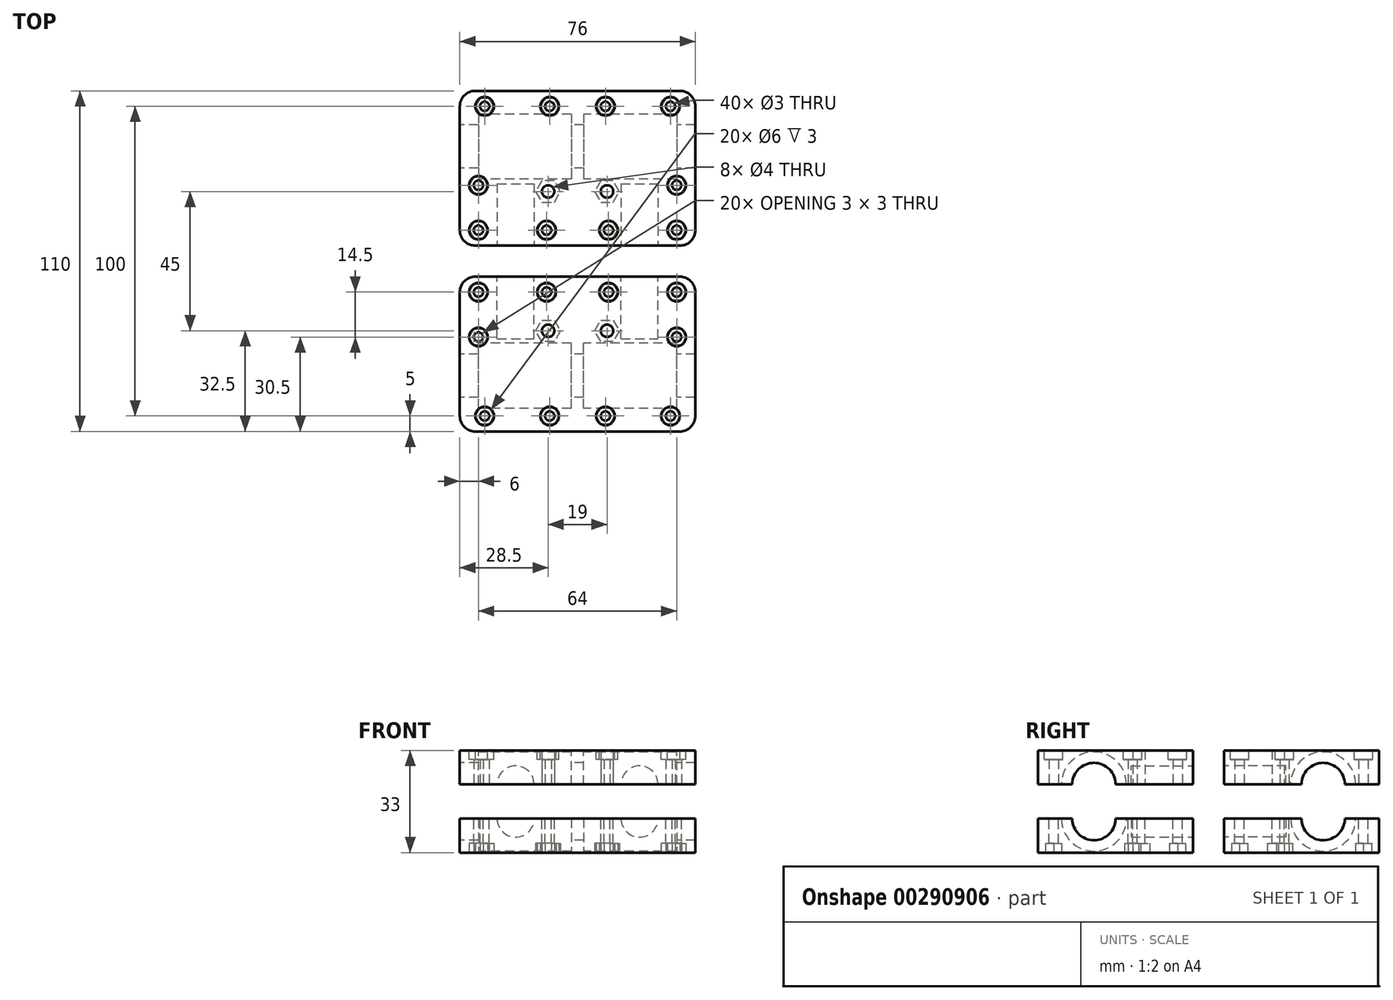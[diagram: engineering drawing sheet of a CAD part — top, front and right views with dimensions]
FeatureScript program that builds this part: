
annotation { "Feature Type Name" : "Feature", "Feature Type Description" : "" }
export const myFeature = defineFeature(function(context is Context, id is Id, definition is map)
    precondition{}
    {
        {
            var Q0;
            Q0=qCreatedBy(makeId("Top.planeOp"),FACE);
            var sketch = newSketch(context, id + "F0", { "sketchPlane" : qUnion([Q0])});
            skLineSegment(sketch, "E0.bottom", {"start": v(38, -25) * mm, "end": v(-38, -25) * mm});
            skLineSegment(sketch, "E0.top", {"start": v(38, 25) * mm, "end": v(-38, 25) * mm});
            skLineSegment(sketch, "E0.left", {"start": v(38, -25) * mm, "end": v(38, 25) * mm});
            skLineSegment(sketch, "E0.right", {"start": v(-38, -25) * mm, "end": v(-38, 25) * mm});
            skPoint(sketch, "E0.middle", {"position": v(0, 0) * mm});
            skSolve(sketch);
        }
        {
            var Q0;
            Q0 = qSketchRegion(id + "F0", true);
            extrude(context, id + "F1", {"entities" : qUnion([Q0]), "endBound" : BoundingType.SYMMETRIC, "depth" : 11 * mm});
        }
        {
            var Q0;
            Q0=makeQuery(id+"F1.opExtrude","CAP_FACE",FACE,{"disambiguationData":[OSD([sQuery(id+"F0.wireOp",EDGE,"E0.bottom"),sQuery(id+"F0.wireOp",EDGE,"E0.top"),sQuery(id+"F0.wireOp",EDGE,"E0.left"),sQuery(id+"F0.wireOp",EDGE,"E0.right")])],"isStart":false});
            var sketch = newSketch(context, id + "F2", { "sketchPlane" : qUnion([Q0])});
            skCircle(sketch, "E1", {"center": v(-30, 20) * mm, "radius": 1.5 * mm});
            skCircle(sketch, "E2", {"center": v(-9, 20) * mm, "radius": 1.5 * mm});
            skCircle(sketch, "E3", {"center": v(9, 20) * mm, "radius": 1.5 * mm});
            skCircle(sketch, "E4", {"center": v(30, 20) * mm, "radius": 1.5 * mm});
            skCircle(sketch, "E5", {"center": v(-32, -20) * mm, "radius": 1.5 * mm});
            skCircle(sketch, "E6", {"center": v(-10, -20) * mm, "radius": 1.5 * mm});
            skCircle(sketch, "E7", {"center": v(10, -20) * mm, "radius": 1.5 * mm});
            skCircle(sketch, "E8", {"center": v(32, -20) * mm, "radius": 1.5 * mm});
            skCircle(sketch, "E9", {"center": v(32, -5.5) * mm, "radius": 1.5 * mm});
            skCircle(sketch, "E10", {"center": v(-9.5, -7.5) * mm, "radius": 2 * mm});
            skCircle(sketch, "E11", {"center": v(9.5, -7.5) * mm, "radius": 2 * mm});
            skCircle(sketch, "E12", {"center": v(-32, -5.5) * mm, "radius": 1.5 * mm});
            skSolve(sketch);
        }
        {
            var Q0;
            Q0 = qSketchRegion(id + "F2", true);
            extrude(context, id + "F3", {"entities" : qUnion([Q0]), "operationType" : NewBodyOperationType.REMOVE, "endBound" : BoundingType.THROUGH_ALL, "oppositeDirection" : true, "depth" : 25 * mm});
        }
        {
            var Q0;
            Q0=makeQuery(id+"F1.opExtrude","SWEPT_FACE",FACE,{"disambiguationData":[OSD([sQuery(id+"F0.wireOp",EDGE,"E0.bottom")])]});
            var sketch = newSketch(context, id + "F4", { "sketchPlane" : qUnion([Q0])});
            skCircle(sketch, "E13", {"center": v(-20, 5.5) * mm, "radius": 6 * mm});
            skCircle(sketch, "E14", {"center": v(20, 5.5) * mm, "radius": 6 * mm});
            skSolve(sketch);
        }
        {
            var Q0;
            Q0 = qSketchRegion(id + "F4", true);
            extrude(context, id + "F5", {"entities" : qUnion([Q0]), "operationType" : NewBodyOperationType.REMOVE, "oppositeDirection" : true, "depth" : 20 * mm});
        }
        {
            var Q0;
            Q0=makeQuery(id+"F1.opExtrude","CAP_FACE",FACE,{"disambiguationData":[OSD([sQuery(id+"F0.wireOp",EDGE,"E0.bottom"),sQuery(id+"F0.wireOp",EDGE,"E0.top"),sQuery(id+"F0.wireOp",EDGE,"E0.left"),sQuery(id+"F0.wireOp",EDGE,"E0.right")])],"isStart":true});
            var sketch = newSketch(context, id + "F6", { "sketchPlane" : qUnion([Q0])});
            skCircle(sketch, "E15.cCircle", {"center": v(-32, 20) * mm, "radius": 2.6 * mm, "construction": true});
            skLineSegment(sketch, "E15.0", {"start": v(-30.5, 17.4) * mm, "end": v(-33.5, 17.4) * mm});
            skLineSegment(sketch, "E15.1", {"start": v(-33.5, 17.4) * mm, "end": v(-35, 20) * mm});
            skLineSegment(sketch, "E15.2", {"start": v(-35, 20) * mm, "end": v(-33.5, 22.6) * mm});
            skLineSegment(sketch, "E15.3", {"start": v(-33.5, 22.6) * mm, "end": v(-30.5, 22.6) * mm});
            skLineSegment(sketch, "E15.4", {"start": v(-30.5, 22.6) * mm, "end": v(-29, 20) * mm});
            skLineSegment(sketch, "E15.5", {"start": v(-29, 20) * mm, "end": v(-30.5, 17.4) * mm});
            skPoint(sketch, "E15.0.midPoint", {"position": v(-32, 17.4) * mm});
            skCircle(sketch, "E16.cCircle", {"center": v(10, 20) * mm, "radius": 2.6 * mm, "construction": true});
            skLineSegment(sketch, "E16.0", {"start": v(11.5, 17.4) * mm, "end": v(8.5, 17.4) * mm});
            skLineSegment(sketch, "E16.1", {"start": v(8.5, 17.4) * mm, "end": v(7, 20) * mm});
            skLineSegment(sketch, "E16.2", {"start": v(7, 20) * mm, "end": v(8.5, 22.6) * mm});
            skLineSegment(sketch, "E16.3", {"start": v(8.5, 22.6) * mm, "end": v(11.5, 22.6) * mm});
            skLineSegment(sketch, "E16.4", {"start": v(11.5, 22.6) * mm, "end": v(13, 20) * mm});
            skLineSegment(sketch, "E16.5", {"start": v(13, 20) * mm, "end": v(11.5, 17.4) * mm});
            skPoint(sketch, "E16.0.midPoint", {"position": v(10, 17.4) * mm});
            skCircle(sketch, "E17.cCircle", {"center": v(-10, 20) * mm, "radius": 2.6 * mm, "construction": true});
            skLineSegment(sketch, "E17.0", {"start": v(-8.5, 17.4) * mm, "end": v(-11.5, 17.4) * mm});
            skLineSegment(sketch, "E17.1", {"start": v(-11.5, 17.4) * mm, "end": v(-13, 20) * mm});
            skLineSegment(sketch, "E17.2", {"start": v(-13, 20) * mm, "end": v(-11.5, 22.6) * mm});
            skLineSegment(sketch, "E17.3", {"start": v(-11.5, 22.6) * mm, "end": v(-8.5, 22.6) * mm});
            skLineSegment(sketch, "E17.4", {"start": v(-8.5, 22.6) * mm, "end": v(-7, 20) * mm});
            skLineSegment(sketch, "E17.5", {"start": v(-7, 20) * mm, "end": v(-8.5, 17.4) * mm});
            skPoint(sketch, "E17.0.midPoint", {"position": v(-10, 17.4) * mm});
            skCircle(sketch, "E18.cCircle", {"center": v(32, 20) * mm, "radius": 2.6 * mm, "construction": true});
            skLineSegment(sketch, "E18.0", {"start": v(33.5, 17.4) * mm, "end": v(30.5, 17.4) * mm});
            skLineSegment(sketch, "E18.1", {"start": v(30.5, 17.4) * mm, "end": v(29, 20) * mm});
            skLineSegment(sketch, "E18.2", {"start": v(29, 20) * mm, "end": v(30.5, 22.6) * mm});
            skLineSegment(sketch, "E18.3", {"start": v(30.5, 22.6) * mm, "end": v(33.5, 22.6) * mm});
            skLineSegment(sketch, "E18.4", {"start": v(33.5, 22.6) * mm, "end": v(35, 20) * mm});
            skLineSegment(sketch, "E18.5", {"start": v(35, 20) * mm, "end": v(33.5, 17.4) * mm});
            skPoint(sketch, "E18.0.midPoint", {"position": v(32, 17.4) * mm});
            skCircle(sketch, "E19.cCircle", {"center": v(-32, 5.5) * mm, "radius": 2.6 * mm, "construction": true});
            skLineSegment(sketch, "E19.0", {"start": v(-30.5, 2.9) * mm, "end": v(-33.5, 2.9) * mm});
            skLineSegment(sketch, "E19.1", {"start": v(-33.5, 2.9) * mm, "end": v(-35, 5.5) * mm});
            skLineSegment(sketch, "E19.2", {"start": v(-35, 5.5) * mm, "end": v(-33.5, 8.1) * mm});
            skLineSegment(sketch, "E19.3", {"start": v(-33.5, 8.1) * mm, "end": v(-30.5, 8.1) * mm});
            skLineSegment(sketch, "E19.4", {"start": v(-30.5, 8.1) * mm, "end": v(-29, 5.5) * mm});
            skLineSegment(sketch, "E19.5", {"start": v(-29, 5.5) * mm, "end": v(-30.5, 2.9) * mm});
            skPoint(sketch, "E19.0.midPoint", {"position": v(-32, 2.9) * mm});
            skCircle(sketch, "E20.cCircle", {"center": v(-30, -20) * mm, "radius": 2.6 * mm, "construction": true});
            skLineSegment(sketch, "E20.0", {"start": v(-28.5, -22.6) * mm, "end": v(-31.5, -22.6) * mm});
            skLineSegment(sketch, "E20.1", {"start": v(-31.5, -22.6) * mm, "end": v(-33, -20) * mm});
            skLineSegment(sketch, "E20.2", {"start": v(-33, -20) * mm, "end": v(-31.5, -17.4) * mm});
            skLineSegment(sketch, "E20.3", {"start": v(-31.5, -17.4) * mm, "end": v(-28.5, -17.4) * mm});
            skLineSegment(sketch, "E20.4", {"start": v(-28.5, -17.4) * mm, "end": v(-27, -20) * mm});
            skLineSegment(sketch, "E20.5", {"start": v(-27, -20) * mm, "end": v(-28.5, -22.6) * mm});
            skPoint(sketch, "E20.0.midPoint", {"position": v(-30, -22.6) * mm});
            skCircle(sketch, "E21.cCircle", {"center": v(-9, -20) * mm, "radius": 2.6 * mm, "construction": true});
            skLineSegment(sketch, "E21.0", {"start": v(-7.5, -22.6) * mm, "end": v(-10.5, -22.6) * mm});
            skLineSegment(sketch, "E21.1", {"start": v(-10.5, -22.6) * mm, "end": v(-12, -20) * mm});
            skLineSegment(sketch, "E21.2", {"start": v(-12, -20) * mm, "end": v(-10.5, -17.4) * mm});
            skLineSegment(sketch, "E21.3", {"start": v(-10.5, -17.4) * mm, "end": v(-7.5, -17.4) * mm});
            skLineSegment(sketch, "E21.4", {"start": v(-7.5, -17.4) * mm, "end": v(-6, -20) * mm});
            skLineSegment(sketch, "E21.5", {"start": v(-6, -20) * mm, "end": v(-7.5, -22.6) * mm});
            skPoint(sketch, "E21.0.midPoint", {"position": v(-9, -22.6) * mm});
            skCircle(sketch, "E22.cCircle", {"center": v(9, -20) * mm, "radius": 2.6 * mm, "construction": true});
            skLineSegment(sketch, "E22.0", {"start": v(10.5, -22.6) * mm, "end": v(7.5, -22.6) * mm});
            skLineSegment(sketch, "E22.1", {"start": v(7.5, -22.6) * mm, "end": v(6, -20) * mm});
            skLineSegment(sketch, "E22.2", {"start": v(6, -20) * mm, "end": v(7.5, -17.4) * mm});
            skLineSegment(sketch, "E22.3", {"start": v(7.5, -17.4) * mm, "end": v(10.5, -17.4) * mm});
            skLineSegment(sketch, "E22.4", {"start": v(10.5, -17.4) * mm, "end": v(12, -20) * mm});
            skLineSegment(sketch, "E22.5", {"start": v(12, -20) * mm, "end": v(10.5, -22.6) * mm});
            skPoint(sketch, "E22.0.midPoint", {"position": v(9, -22.6) * mm});
            skCircle(sketch, "E23.cCircle", {"center": v(30, -20) * mm, "radius": 2.6 * mm, "construction": true});
            skLineSegment(sketch, "E23.0", {"start": v(31.5, -22.6) * mm, "end": v(28.5, -22.6) * mm});
            skLineSegment(sketch, "E23.1", {"start": v(28.5, -22.6) * mm, "end": v(27, -20) * mm});
            skLineSegment(sketch, "E23.2", {"start": v(27, -20) * mm, "end": v(28.5, -17.4) * mm});
            skLineSegment(sketch, "E23.3", {"start": v(28.5, -17.4) * mm, "end": v(31.5, -17.4) * mm});
            skLineSegment(sketch, "E23.4", {"start": v(31.5, -17.4) * mm, "end": v(33, -20) * mm});
            skLineSegment(sketch, "E23.5", {"start": v(33, -20) * mm, "end": v(31.5, -22.6) * mm});
            skPoint(sketch, "E23.0.midPoint", {"position": v(30, -22.6) * mm});
            skCircle(sketch, "E24.cCircle", {"center": v(32, 5.5) * mm, "radius": 2.6 * mm, "construction": true});
            skLineSegment(sketch, "E24.0", {"start": v(33.5, 2.9) * mm, "end": v(30.5, 2.9) * mm});
            skLineSegment(sketch, "E24.1", {"start": v(30.5, 2.9) * mm, "end": v(29, 5.5) * mm});
            skLineSegment(sketch, "E24.2", {"start": v(29, 5.5) * mm, "end": v(30.5, 8.1) * mm});
            skLineSegment(sketch, "E24.3", {"start": v(30.5, 8.1) * mm, "end": v(33.5, 8.1) * mm});
            skLineSegment(sketch, "E24.4", {"start": v(33.5, 8.1) * mm, "end": v(35, 5.5) * mm});
            skLineSegment(sketch, "E24.5", {"start": v(35, 5.5) * mm, "end": v(33.5, 2.9) * mm});
            skPoint(sketch, "E24.0.midPoint", {"position": v(32, 2.9) * mm});
            skSolve(sketch);
        }
        {
            var Q0;
            Q0 = qSketchRegion(id + "F6", true);
            extrude(context, id + "F7", {"entities" : qUnion([Q0]), "operationType" : NewBodyOperationType.REMOVE, "oppositeDirection" : true, "depth" : 3 * mm});
        }
        {
            var Q0;
            Q0=makeQuery(id+"F1.opExtrude","SWEPT_FACE",FACE,{"disambiguationData":[OSD([sQuery(id+"F0.wireOp",EDGE,"E0.right")])]});
            var sketch = newSketch(context, id + "F8", { "sketchPlane" : qUnion([Q0])});
            skCircle(sketch, "E25", {"center": v(-7, 5.5) * mm, "radius": 7 * mm});
            skSolve(sketch);
        }
        {
            var Q0;
            Q0 = qSketchRegion(id + "F8", true);
            extrude(context, id + "F9", {"entities" : qUnion([Q0]), "operationType" : NewBodyOperationType.REMOVE, "endBound" : BoundingType.THROUGH_ALL, "oppositeDirection" : true, "depth" : 25 * mm});
        }
        {
            var Q0;
            Q0=makeQuery(id+"F1.opExtrude","SWEPT_FACE",FACE,{"disambiguationData":[OSD([sQuery(id+"F0.wireOp",EDGE,"E0.right")])]});
            var sketch = newSketch(context, id + "F10", { "sketchPlane" : qUnion([Q0])});
            skCircle(sketch, "E26", {"center": v(-7, 5.5) * mm, "radius": 10.5 * mm});
            skSolve(sketch);
        }
        {
            var Q0;
            Q0 = qSketchRegion(id + "F10", true);
            extrude(context, id + "F11", {"entities" : qUnion([Q0]), "operationType" : NewBodyOperationType.REMOVE, "oppositeDirection" : true, "depth" : 36 * mm, "hasSecondDirection" : true, "secondDirectionOppositeDirection" : true, "secondDirectionDepth" : 6 * mm});
        }
        {
            var Q0;
            Q0=makeQuery(id+"F1.opExtrude","SWEPT_EDGE",EDGE,{"disambiguationData":[OSD([sQuery(id+"F0.wireOp",EDGE,"E0.bottom"),sQuery(id+"F0.wireOp",EDGE,"E0.left")])]});
            var Q1;
            Q1=makeQuery(id+"F1.opExtrude","SWEPT_EDGE",EDGE,{"disambiguationData":[OSD([sQuery(id+"F0.wireOp",EDGE,"E0.bottom"),sQuery(id+"F0.wireOp",EDGE,"E0.right")])]});
            var Q2;
            Q2=makeQuery(id+"F1.opExtrude","SWEPT_EDGE",EDGE,{"disambiguationData":[OSD([sQuery(id+"F0.wireOp",EDGE,"E0.top"),sQuery(id+"F0.wireOp",EDGE,"E0.right")])]});
            var Q3;
            Q3=makeQuery(id+"F1.opExtrude","SWEPT_EDGE",EDGE,{"disambiguationData":[OSD([sQuery(id+"F0.wireOp",EDGE,"E0.top"),sQuery(id+"F0.wireOp",EDGE,"E0.left")])]});
            fillet(context, id + "F12", {"entities" : qUnion([Q0, Q1, Q2, Q3]), "radius" : 5 * mm, "tangentPropagation" : true, "allowEdgeOverflow" : false});
        }
        {
            var Q0;
            Q0 = qSketchRegion(id + "F10", true);
            extrude(context, id + "F13", {"entities" : qUnion([Q0]), "operationType" : NewBodyOperationType.REMOVE, "oppositeDirection" : true, "depth" : 70 * mm, "hasSecondDirection" : true, "secondDirectionOppositeDirection" : true, "secondDirectionDepth" : 40 * mm});
        }
        {
            var Q0;
            Q0=qCreatedBy(makeId("Top.planeOp"),FACE);
            cPlane(context, id + "F14", {"entities" : qUnion([Q0]), "cplaneType" : CPlaneType.OFFSET, "offset" : 11 * mm, "width" : 150 * mm, "height" : 150 * mm});
        }
        {
            var Q0;
            Q0=makeQuery(id+"F1.opExtrude","SWEPT_BODY",BODY,{"disambiguationData":[OSD([sQuery(id+"F0.wireOp",EDGE,"E0.bottom"),sQuery(id+"F0.wireOp",EDGE,"E0.top"),sQuery(id+"F0.wireOp",EDGE,"E0.left"),sQuery(id+"F0.wireOp",EDGE,"E0.right")])]});
            var Q1;
            Q1=qCreatedBy(id+"F14.planeOp",FACE);
            mirror(context, id + "F15", {"entities" : qUnion([Q0]), "mirrorPlane" : qUnion([Q1])});
        }
        {
            var Q0;
            Q0=makeQuery(id+"F15.opPattern","COPY",FACE,{"derivedFrom":makeQuery(id+"F1.opExtrude","CAP_FACE",FACE,{"disambiguationData":[OSD([sQuery(id+"F0.wireOp",EDGE,"E0.bottom"),sQuery(id+"F0.wireOp",EDGE,"E0.top"),sQuery(id+"F0.wireOp",EDGE,"E0.left"),sQuery(id+"F0.wireOp",EDGE,"E0.right")])],"isStart":true}),"instanceName":"1"});
            var sketch = newSketch(context, id + "F16", { "sketchPlane" : qUnion([Q0])});
            skCircle(sketch, "E27", {"center": v(-30, 20) * mm, "radius": 3 * mm});
            skCircle(sketch, "E28", {"center": v(-9, 20) * mm, "radius": 3 * mm});
            skCircle(sketch, "E29", {"center": v(-49.47, 3.97) * mm, "radius": 3 * mm});
            skCircle(sketch, "E30", {"center": v(-32, -5.5) * mm, "radius": 3 * mm});
            skCircle(sketch, "E31", {"center": v(-32, -20) * mm, "radius": 3 * mm});
            skCircle(sketch, "E32", {"center": v(32, -5.5) * mm, "radius": 3 * mm});
            skCircle(sketch, "E33", {"center": v(32, -20) * mm, "radius": 3 * mm});
            skCircle(sketch, "E34", {"center": v(10, -20) * mm, "radius": 3 * mm});
            skCircle(sketch, "E35", {"center": v(-10, -20) * mm, "radius": 3 * mm});
            skCircle(sketch, "E36", {"center": v(30, 20) * mm, "radius": 3 * mm});
            skCircle(sketch, "E37", {"center": v(9, 20) * mm, "radius": 3 * mm});
            skSolve(sketch);
        }
        {
            var Q0;
            Q0 = qSketchRegion(id + "F16", true);
            extrude(context, id + "F17", {"entities" : qUnion([Q0]), "operationType" : NewBodyOperationType.REMOVE, "oppositeDirection" : true, "depth" : 3 * mm});
        }
        {
            var Q0;
            Q0=makeQuery(id+"F6.imprint","IMPRINT",FACE,{"disambiguationData":[TD([[makeQuery(id+"F6.imprint","IMPRINT",EDGE,{"derivedFrom":sQuery(id+"F6.wireOp",EDGE,"E15.0")}),1.0]])]});
            var sketch = newSketch(context, id + "F18", { "sketchPlane" : qUnion([Q0])});
            skCircle(sketch, "E38.cCircle", {"center": v(-9.5, 7.5) * mm, "radius": 3.46 * mm, "construction": true});
            skLineSegment(sketch, "E38.0", {"start": v(-7.5, 4.04) * mm, "end": v(-11.5, 4.04) * mm});
            skLineSegment(sketch, "E38.1", {"start": v(-11.5, 4.04) * mm, "end": v(-13.5, 7.5) * mm});
            skLineSegment(sketch, "E38.2", {"start": v(-13.5, 7.5) * mm, "end": v(-11.5, 10.96) * mm});
            skLineSegment(sketch, "E38.3", {"start": v(-11.5, 10.96) * mm, "end": v(-7.5, 10.96) * mm});
            skLineSegment(sketch, "E38.4", {"start": v(-7.5, 10.96) * mm, "end": v(-5.5, 7.5) * mm});
            skLineSegment(sketch, "E38.5", {"start": v(-5.5, 7.5) * mm, "end": v(-7.5, 4.04) * mm});
            skPoint(sketch, "E38.0.midPoint", {"position": v(-9.5, 4.04) * mm});
            skCircle(sketch, "E39.cCircle", {"center": v(9.5, 7.5) * mm, "radius": 3.46 * mm, "construction": true});
            skLineSegment(sketch, "E39.0", {"start": v(11.5, 4.04) * mm, "end": v(7.5, 4.04) * mm});
            skLineSegment(sketch, "E39.1", {"start": v(7.5, 4.04) * mm, "end": v(5.5, 7.5) * mm});
            skLineSegment(sketch, "E39.2", {"start": v(5.5, 7.5) * mm, "end": v(7.5, 10.96) * mm});
            skLineSegment(sketch, "E39.3", {"start": v(7.5, 10.96) * mm, "end": v(11.5, 10.96) * mm});
            skLineSegment(sketch, "E39.4", {"start": v(11.5, 10.96) * mm, "end": v(13.5, 7.5) * mm});
            skLineSegment(sketch, "E39.5", {"start": v(13.5, 7.5) * mm, "end": v(11.5, 4.04) * mm});
            skPoint(sketch, "E39.0.midPoint", {"position": v(9.5, 4.04) * mm});
            skSolve(sketch);
        }
        {
            var Q0;
            Q0 = qSketchRegion(id + "F18", true);
            extrude(context, id + "F19", {"entities" : qUnion([Q0]), "operationType" : NewBodyOperationType.REMOVE, "oppositeDirection" : true, "depth" : 3 * mm});
        }
        {
            var Q0;
            Q0=qCreatedBy(makeId("Front.planeOp"),FACE);
            cPlane(context, id + "F20", {"entities" : qUnion([Q0]), "cplaneType" : CPlaneType.OFFSET, "offset" : 30 * mm, "width" : 150 * mm, "height" : 150 * mm});
        }
        {
            var Q0;
            Q0=makeQuery(id+"F15.opPattern","COPY",BODY,{"derivedFrom":makeQuery(id+"F1.opExtrude","SWEPT_BODY",BODY,{"disambiguationData":[OSD([sQuery(id+"F0.wireOp",EDGE,"E0.bottom"),sQuery(id+"F0.wireOp",EDGE,"E0.top"),sQuery(id+"F0.wireOp",EDGE,"E0.left"),sQuery(id+"F0.wireOp",EDGE,"E0.right")])]}),"instanceName":"1"});
            var Q1;
            Q1=makeQuery(id+"F1.opExtrude","SWEPT_BODY",BODY,{"disambiguationData":[OSD([sQuery(id+"F0.wireOp",EDGE,"E0.bottom"),sQuery(id+"F0.wireOp",EDGE,"E0.top"),sQuery(id+"F0.wireOp",EDGE,"E0.left"),sQuery(id+"F0.wireOp",EDGE,"E0.right")])]});
            var Q2;
            Q2=qCreatedBy(id+"F20.planeOp",FACE);
            mirror(context, id + "F21", {"entities" : qUnion([Q0, Q1]), "mirrorPlane" : qUnion([Q2])});
        }
    });
